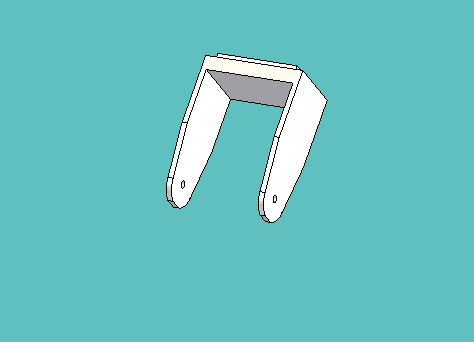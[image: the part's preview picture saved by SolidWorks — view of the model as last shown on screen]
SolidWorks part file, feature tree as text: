
SOLIDWORKS PART (.sldprt)
format: sldprt  version: not decoded by parser v0  size: 317,952 bytes
history: native  units: mm
features: sketch x5, extrude x4, material x1 (+11 scaffold rows collapsed)
feature tree (21):
  scaffold x11  (default folders/planes/origin — collapsed)
  material  "Material <not specified>"
  sketch  "Sketch1"  dims[D1=38.1mm D2=25.4mm]
  extrude  "Extrude1"  Depth=2.38125mm
  sketch  "Sketch2"  dims[D1=1.5875mm D2=1.5875mm D3=4.2672mm D4=4.2672mm]
  extrude  "Extrude2"  Depth=6.35mm
  sketch  "Sketch3"  dims[D2=3.175mm D7=22.225mm D1=47.625mm D3=9.525mm D4=6.35mm D5=25.4mm D6=23.8125mm]
  extrude  "Extrude3"  Depth=2.4892mm
  sketch  "Sketch4"  dims[D1=0.0mm]
  extrude  "Extrude4"  Depth=2.4892mm
  sketch  "Sketch5"  dims[D1=36.068mm D2=0.0mm]
decode coverage: 9 of 9 modeling features carry decoded parameters
note: suppression state not decoded; provenance and decode notes live in map.json
